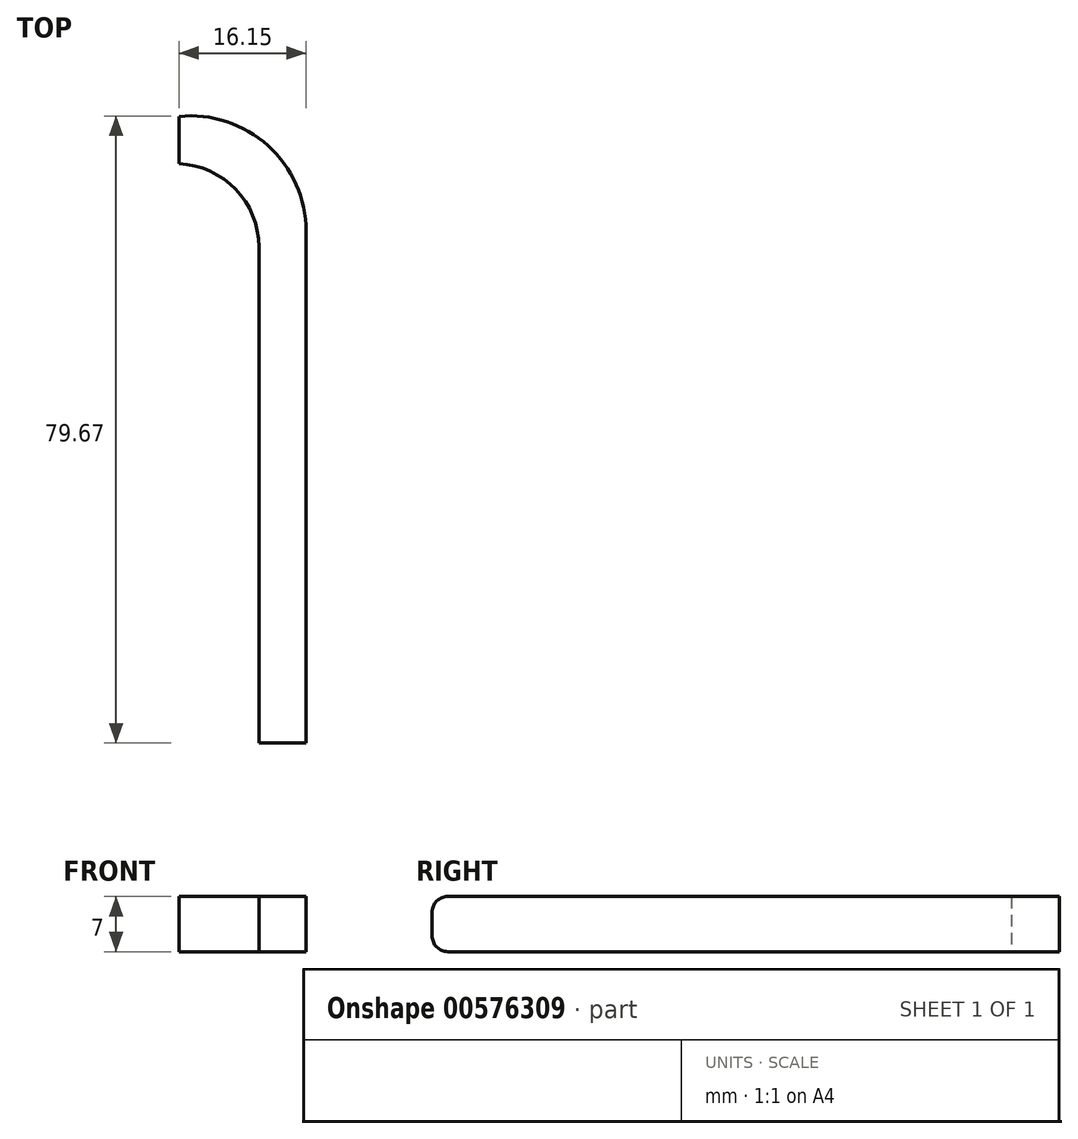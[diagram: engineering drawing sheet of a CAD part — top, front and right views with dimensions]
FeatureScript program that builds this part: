
annotation { "Feature Type Name" : "Feature", "Feature Type Description" : "" }
export const myFeature = defineFeature(function(context is Context, id is Id, definition is map)
    precondition{}
    {
        {
            var Q0;
            Q0=qCreatedBy(makeId("Top.planeOp"),FACE);
            var sketch = newSketch(context, id + "F0", { "sketchPlane" : qUnion([Q0])});
            skLineSegment(sketch, "E0", {"start": v(0, -5.8) * mm, "end": v(3, -5.8) * mm});
            skLineSegment(sketch, "E1", {"start": v(0, -5.8) * mm, "end": v(-3, -5.8) * mm});
            skLineSegment(sketch, "E2", {"start": v(3, -5.8) * mm, "end": v(3, 59.2) * mm});
            skLineSegment(sketch, "E3", {"start": v(-3, -5.8) * mm, "end": v(-3, 57.2) * mm});
            skLineSegment(sketch, "E4", {"start": v(-3, 57.2) * mm, "end": v(-3, 81.96) * mm, "construction": true});
            skLineSegment(sketch, "E5", {"start": v(3, 59.2) * mm, "end": v(3, 84.36) * mm, "construction": true});
            skArc(sketch, "E6", {"start": v(3, 59.2) * mm, "mid": v(-1.83, 70.09) * mm, "end": v(-13.15, 73.8) * mm});
            skArc(sketch, "E7", {"start": v(-3, 57.2) * mm, "mid": v(-5.95, 64.54) * mm, "end": v(-13.15, 67.8) * mm});
            skLineSegment(sketch, "E8", {"start": v(-13.15, 73.8) * mm, "end": v(-13.15, 76.3) * mm});
            skLineSegment(sketch, "E9", {"start": v(-13.15, 67.8) * mm, "end": v(-13.15, 65.8) * mm});
            skLineSegment(sketch, "E10", {"start": v(-13.15, 76.3) * mm, "end": v(-16.15, 76.3) * mm});
            skLineSegment(sketch, "E11", {"start": v(-13.15, 65.8) * mm, "end": v(-16.15, 65.8) * mm});
            skLineSegment(sketch, "E12", {"start": v(-16.15, 65.8) * mm, "end": v(-16.15, 69.3) * mm});
            skLineSegment(sketch, "E13", {"start": v(-16.15, 76.3) * mm, "end": v(-16.15, 72.3) * mm});
            skEllipse(sketch, "E14", {"center": v(-20.8, 70.8) * mm, "majorRadius": 2.84 * mm, "minorRadius": 1.35 * mm, "majorAxis": v(0, -1)});
            skLineSegment(sketch, "E15", {"start": v(-16.15, 72.3) * mm, "end": v(-19.65, 72.3) * mm});
            skLineSegment(sketch, "E16", {"start": v(-16.15, 69.3) * mm, "end": v(-19.65, 69.3) * mm});
            skLineSegment(sketch, "E17", {"start": v(-13.15, 73.8) * mm, "end": v(-13.15, 67.8) * mm});
            skSolve(sketch);
        }
        {
            var Q0;
            Q0=makeQuery(id+"F0.imprint","IMPRINT",FACE,{"disambiguationData":[TD([[makeQuery(id+"F0.imprint","IMPRINT",EDGE,{"derivedFrom":sQuery(id+"F0.wireOp",EDGE,"E0")}),1.0]])]});
            extrude(context, id + "F1", {"entities" : qUnion([Q0]), "depth" : 7 * mm, "offsetDistance" : 25 * mm});
        }
        {
            var Q0;
            Q0=makeQuery(id+"F1.opExtrude","CAP_EDGE",EDGE,{"disambiguationData":[OSD([sQuery(id+"F0.wireOp",EDGE,"E0"),sQuery(id+"F0.wireOp",EDGE,"E1")])],"isStart":false});
            var Q1;
            Q1=makeQuery(id+"F1.opExtrude","CAP_EDGE",EDGE,{"disambiguationData":[OSD([sQuery(id+"F0.wireOp",EDGE,"E0"),sQuery(id+"F0.wireOp",EDGE,"E1")])],"isStart":true});
            fillet(context, id + "F2", {"entities" : qUnion([Q0, Q1]), "radius" : 2 * mm, "tangentPropagation" : true, "allowEdgeOverflow" : false});
        }
    });
